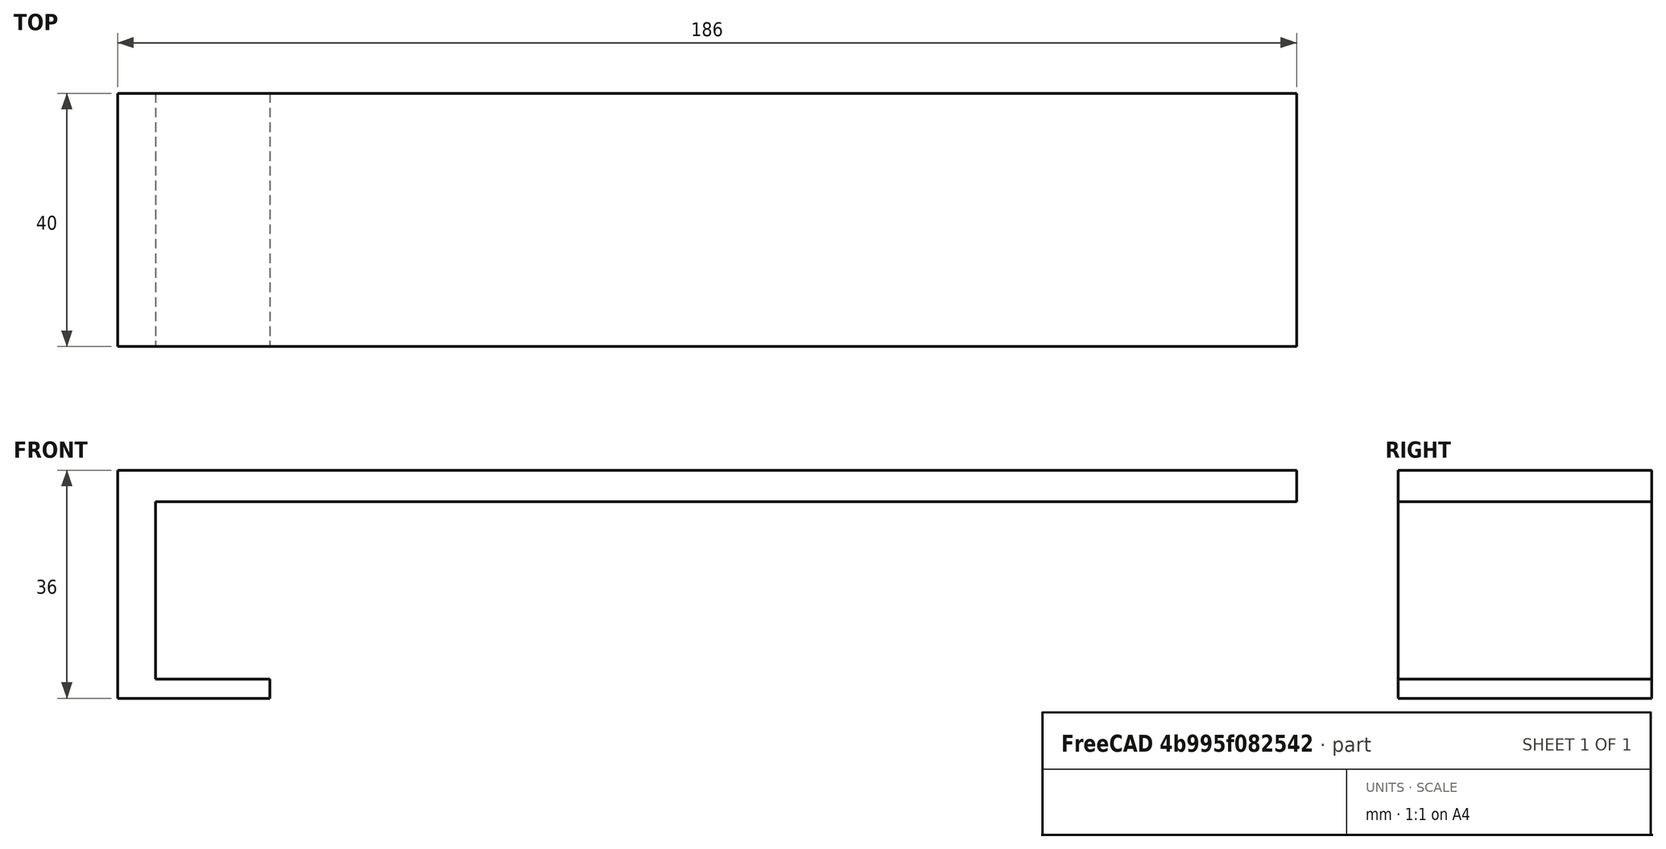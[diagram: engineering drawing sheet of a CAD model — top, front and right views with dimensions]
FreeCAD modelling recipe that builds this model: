
FCSTD DOCUMENT  (FreeCAD 1.0R39319 (Git))
Label: poolcover_side
License: All rights reserved
LicenseURL: https://en.wikipedia.org/wiki/All_rights_reserved
objects: Sketcher::SketchObject×2, PartDesign::Body×2, PartDesign::Pad×1
note: 9 computed .brp shape members not serialized (recipe doc carries the construction recipe); baked Part::Feature solids carry a one-line shape summary decoded from their .brp

FEATURE [Sketcher::SketchObject] Sketch
  ArcFitTolerance = 1e-06
  AttachmentSupport = -> [XZ_Plane]
  FullyConstrained = true
  MakeInternals = false
  MapMode = 5
  Placement = pos=(0,0,0) rot=(1,0,0;1.5708rad)
FEATURE [PartDesign::Body] Body
  AllowCompound = false
  Group = -> [Sketch]
  Origin = -> Origin
FEATURE [Sketcher::SketchObject] Sketch001
  ArcFitTolerance = 1e-06
  AttachmentSupport = -> [XZ_Plane001]
  FullyConstrained = true
  MakeInternals = false
  MapMode = 5
  Placement = pos=(0,0,0) rot=(1,0,0;1.5708rad)
  sketch-geometry (8):
    g0: LineSegment StartX=0 StartY=0 StartZ=0 EndX=180 EndY=0 EndZ=0
    g1: LineSegment StartX=0 StartY=0 StartZ=0 EndX=0 EndY=-28 EndZ=0
    g2: LineSegment StartX=0 StartY=-28 StartZ=0 EndX=18 EndY=-28 EndZ=0
    g3: LineSegment StartX=18 StartY=-28 StartZ=0 EndX=18 EndY=-31 EndZ=0
    g4: LineSegment StartX=18 StartY=-31 StartZ=0 EndX=-6 EndY=-31 EndZ=0
    g5: LineSegment StartX=-6 StartY=-31 StartZ=0 EndX=-6 EndY=5 EndZ=0
    g6: LineSegment StartX=-6 StartY=5 StartZ=0 EndX=180 EndY=5 EndZ=0
    g7: LineSegment StartX=180 StartY=5 StartZ=0 EndX=180 EndY=0 EndZ=0
  constraints (23):
    c: Distance(g0) = 180
    c: Coincident(g0,g-1)
    c: Horizontal(g0)
    c: Distance(g1) = 28
    c: Coincident(g1,g0)
    c: PointOnObject(g1,g-2)
    c: Distance(g2) = 18
    c: Coincident(g2,g1)
    c: Horizontal(g2)
    c: Distance(g3) = 3
    c: Coincident(g3,g2)
    c: Vertical(g3)
    c: Distance(g4) = 24
    c: Coincident(g4,g3)
    c: Horizontal(g4)
    c: Distance(g5) = 36
    c: Coincident(g5,g4)
    c: Vertical(g5)
    c: Distance(g6) = 186
    c: Coincident(g6,g5)
    c: Horizontal(g6)
    c: Coincident(g7,g6)
    c: Coincident(g7,g0)
FEATURE [PartDesign::Pad] Pad
  Direction = (0,-1,2e-16)
  Length = 40
  Length2 = 10
  Placement = pos=(0,0,0) rot=(1,0,0;1.5708rad)
  Profile = -> Sketch001
  ReferenceAxis = -> Sketch001 [N_Axis]
  Refine = true
  Suppressed = false
  Type = 0
FEATURE [PartDesign::Body] Body001
  AllowCompound = false
  Group = -> [Sketch001,Pad]
  Origin = -> Origin001
  Tip = -> Pad
